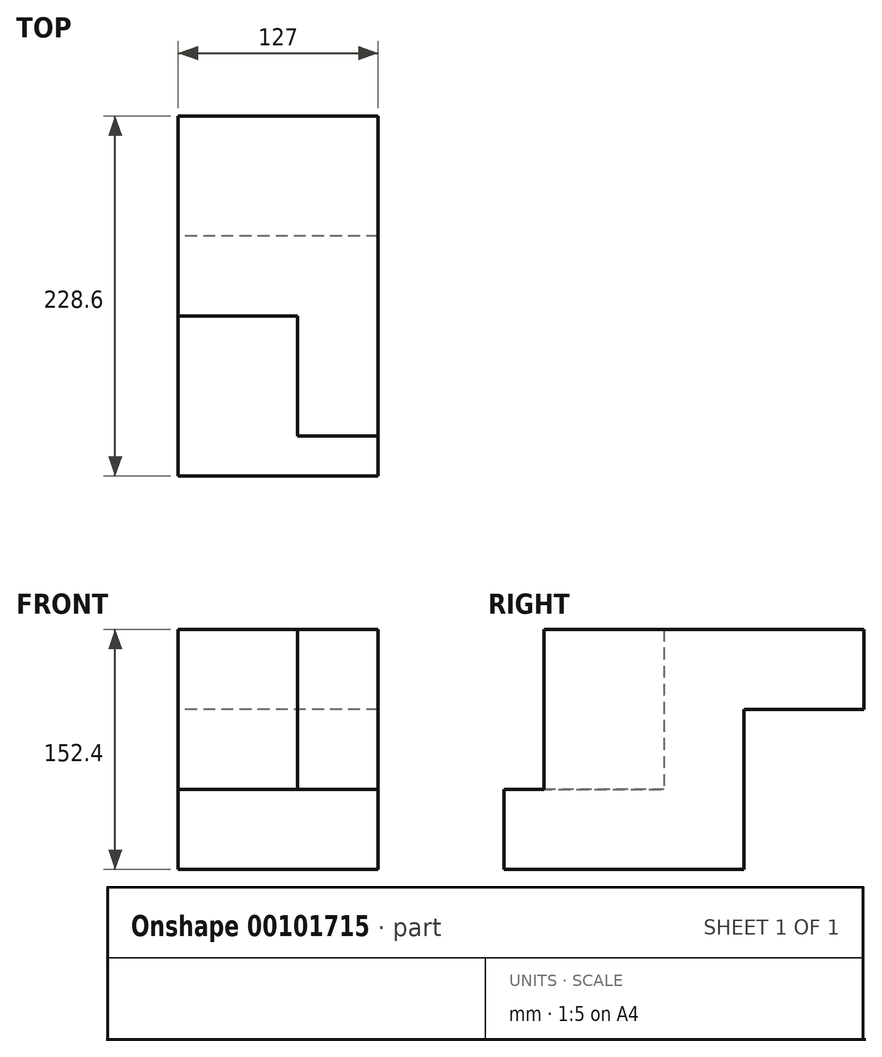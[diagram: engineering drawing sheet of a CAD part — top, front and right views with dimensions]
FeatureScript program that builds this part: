
annotation { "Feature Type Name" : "Feature", "Feature Type Description" : "" }
export const myFeature = defineFeature(function(context is Context, id is Id, definition is map)
    precondition{}
    {
        {
            var Q0;
            Q0=qCreatedBy(makeId("Front.planeOp"),FACE);
            var sketch = newSketch(context, id + "F0", { "sketchPlane" : qUnion([Q0])});
            skLineSegment(sketch, "E0", {"start": v(-75.77, -36.33) * mm, "end": v(-75.77, -87.13) * mm});
            skLineSegment(sketch, "E1", {"start": v(-75.77, -87.13) * mm, "end": v(51.23, -87.13) * mm});
            skLineSegment(sketch, "E2", {"start": v(51.23, -87.13) * mm, "end": v(51.23, -36.33) * mm});
            skLineSegment(sketch, "E3", {"start": v(51.23, -36.33) * mm, "end": v(-75.77, -36.33) * mm});
            skSolve(sketch);
        }
        {
            var Q0;
            Q0=makeQuery(id+"F0.imprint","IMPRINT",FACE,{"disambiguationData":[TD([[makeQuery(id+"F0.imprint","IMPRINT",EDGE,{"derivedFrom":sQuery(id+"F0.wireOp",EDGE,"E0")}),1.0]])]});
            extrude(context, id + "F1", {"entities" : qUnion([Q0]), "depth" : 152.4 * mm});
        }
        {
            var Q0;
            Q0=makeQuery(id+"F1.opExtrude","SWEPT_FACE",FACE,{"disambiguationData":[OSD([sQuery(id+"F0.wireOp",EDGE,"E3")])]});
            var sketch = newSketch(context, id + "F2", { "sketchPlane" : qUnion([Q0])});
            skLineSegment(sketch, "E4.bottom", {"start": v(-75.77, 0) * mm, "end": v(0.43, 0) * mm});
            skLineSegment(sketch, "E4.top", {"start": v(-75.77, -50.8) * mm, "end": v(0.43, -50.8) * mm});
            skLineSegment(sketch, "E4.left", {"start": v(-75.77, 0) * mm, "end": v(-75.77, -50.8) * mm});
            skLineSegment(sketch, "E4.right", {"start": v(0.43, 0) * mm, "end": v(0.43, -50.8) * mm});
            skSolve(sketch);
        }
        {
            var Q0;
            Q0=makeQuery(id+"F2.imprint","IMPRINT",FACE,{"disambiguationData":[TD([[makeQuery(id+"F2.imprint","IMPRINT",EDGE,{"derivedFrom":sQuery(id+"F2.wireOp",EDGE,"E4.bottom")}),1.0]])]});
            extrude(context, id + "F3", {"entities" : qUnion([Q0]), "operationType" : NewBodyOperationType.ADD, "depth" : 101.6 * mm});
        }
        {
            var Q0;
            Q0=makeQuery(id+"F1.opExtrude","SWEPT_FACE",FACE,{"disambiguationData":[OSD([sQuery(id+"F0.wireOp",EDGE,"E3")])]});
            var sketch = newSketch(context, id + "F4", { "sketchPlane" : qUnion([Q0])});
            skLineSegment(sketch, "E5.bottom", {"start": v(51.23, 0) * mm, "end": v(0, 0) * mm});
            skLineSegment(sketch, "E5.top", {"start": v(51.23, -127) * mm, "end": v(0, -127) * mm});
            skLineSegment(sketch, "E5.left", {"start": v(51.23, 0) * mm, "end": v(51.23, -127) * mm});
            skLineSegment(sketch, "E5.right", {"start": v(0, 0) * mm, "end": v(0, -127) * mm});
            skSolve(sketch);
        }
        {
            var Q0;
            {var subQ1=sQuery(id+"F4.wireOp",EDGE,"E5.top");Q0=makeQuery(id+"F4.imprint","IMPRINT",FACE,{"disambiguationData":[TD([[makeQuery(id+"F4.imprint","IMPRINT",EDGE,{"derivedFrom":subQ1}),-1.0]])]});}
            extrude(context, id + "F5", {"entities" : qUnion([Q0]), "operationType" : NewBodyOperationType.ADD, "depth" : 101.6 * mm});
        }
        {
            var Q0;
            Q0=makeQuery(id+"F5.boolean.opBoolean","MERGE",FACE,{"derivedFrom":[makeQuery(id+"F3.boolean.opBoolean","MERGE",FACE,{"derivedFrom":[makeQuery(id+"F1.opExtrude","CAP_FACE",FACE,{"disambiguationData":[OSD([sQuery(id+"F0.wireOp",EDGE,"E0"),sQuery(id+"F0.wireOp",EDGE,"E1"),sQuery(id+"F0.wireOp",EDGE,"E2"),sQuery(id+"F0.wireOp",EDGE,"E3")])],"isStart":true}),makeQuery(id+"F3.opExtrude","SWEPT_FACE",FACE,{"disambiguationData":[OSD([sQuery(id+"F2.wireOp",EDGE,"E4.bottom")])]})]}),makeQuery(id+"F5.opExtrude","SWEPT_FACE",FACE,{"disambiguationData":[OSD([sQuery(id+"F4.wireOp",EDGE,"E5.bottom")])]})]});
            var sketch = newSketch(context, id + "F6", { "sketchPlane" : qUnion([Q0])});
            skLineSegment(sketch, "E6.bottom", {"start": v(-51.23, 65.27) * mm, "end": v(75.77, 65.27) * mm});
            skLineSegment(sketch, "E6.top", {"start": v(-51.23, 14.47) * mm, "end": v(75.77, 14.47) * mm});
            skLineSegment(sketch, "E6.left", {"start": v(-51.23, 65.27) * mm, "end": v(-51.23, 14.47) * mm});
            skLineSegment(sketch, "E6.right", {"start": v(75.77, 65.27) * mm, "end": v(75.77, 14.47) * mm});
            skSolve(sketch);
        }
        {
            var Q0;
            Q0=makeQuery(id+"F6.imprint","IMPRINT",FACE,{"disambiguationData":[TD([[makeQuery(id+"F6.imprint","IMPRINT",EDGE,{"derivedFrom":sQuery(id+"F6.wireOp",EDGE,"E6.bottom")}),-1.0]])]});
            extrude(context, id + "F7", {"entities" : qUnion([Q0]), "operationType" : NewBodyOperationType.ADD, "depth" : 76.2 * mm});
        }
    });
